# Revit family: FT Mustang_2020
name_source: partatom
category: Lighting Fixtures
units: mm (PartAtom-declared; Revit-internal decimal feet)

## family parameters
Always vertical = Yes
Cut with Voids When Loaded = No
Light Source = Yes
OmniClass Number = 23.80.70.00
OmniClass Title = Lighting
Part Type = Normal
Room Calculation Point = No
Round Connector Dimension = Use Diameter
Shared = No
Work Plane-Based = No

## types (12) — shared parameters
Chromatic Index = CR>80
Color Filter = 16777215
Description = https://www.airfal.com
Dimming Lamp Color Temperature Shift = <None>
Emergency system = No
Emit from Line Length = 609.6 mm  [stored 2 ft]
IK = IK10
IP = IP69K
Led Module = Yes
MacAdam Ellipse = 3/4
Photobiological risk group = RG 0/1
URL = https://www.airfal.com
Unify glade rating = UGR<19
Useful life = L70B50>50000
zero-valued in all types: Default Elevation

## per-type parameters (varying)
| type | L | Net output | Photometric Web File | Size | Tilt Angle | Watts |
| MU113 | 763 mm | 997 lm | generic | 600 mm | 60.00° | 13 W |
| MU114 | 763 mm | 1037 lm | generic | 600 mm | 60.00° | 13 W |
| MU123 | 763 mm | 1712 lm | MU123 MUSTANG 16W 3000K 2650 lm G5.IES | 600 mm | 90.00° | 16 W |
| MU124 | 763 mm | 1786 lm | MU124 MUSTANG 16W 4000K 2775 lm G5.IES | 600 mm | 90.00° | 16 W |
| MU213 | 1375 mm  [stored 4.51115 ft] | 1993 lm | generic | 1200 mm | 60.00° | 24 W |
| MU214 | 1375 mm  [stored 4.51115 ft] | 2140 lm | generic | 1200 mm | 60.00° | 24 W |
| MU223 | 1375 mm  [stored 4.51115 ft] | 3424 lm | MU223 MUSTANG 1200 32W 3000K 5300 lm G5.IES | 1200 mm | 90.00° | 32 W |
| MU313 | 1660 mm  [stored 5.44619 ft] | 2488 lm | generic | 1500 mm  [stored 4.92126 ft] | 60.00° | 29 W |
| MU224 | 1375 mm  [stored 4.51115 ft] | 3571 lm | MU224 MUSTANG 1200 32W 4000K 5550 lm G5.IES | 1200 mm | 90.00° | 32 W |
| MU314 | 1660 mm  [stored 5.44619 ft] | 2675 lm | generic | 1500 mm  [stored 4.92126 ft] | 60.00° | 29 W |
| MU323 | 1660 mm  [stored 5.44619 ft] | 4220 lm | MU323 MUSTANG 1500 40W 3000K 6631 lm G5.IES | 1500 mm  [stored 4.92126 ft] | 90.00° | 40 W |
| MU324 | 1660 mm  [stored 5.44619 ft] | 4481 lm | MU324 MUSTANG 1500 40W 4000K 6940 lm G5.IES | 1500 mm  [stored 4.92126 ft] | 90.00° | 40 W |

note: [stored X ft] marks values corroborated as IEEE doubles in the binary element streams (Revit-internal decimal feet)

## geometry (parser evidence)
native form markers: Blend x8, Sweep x20
no freeform markers — native parametric forms only
